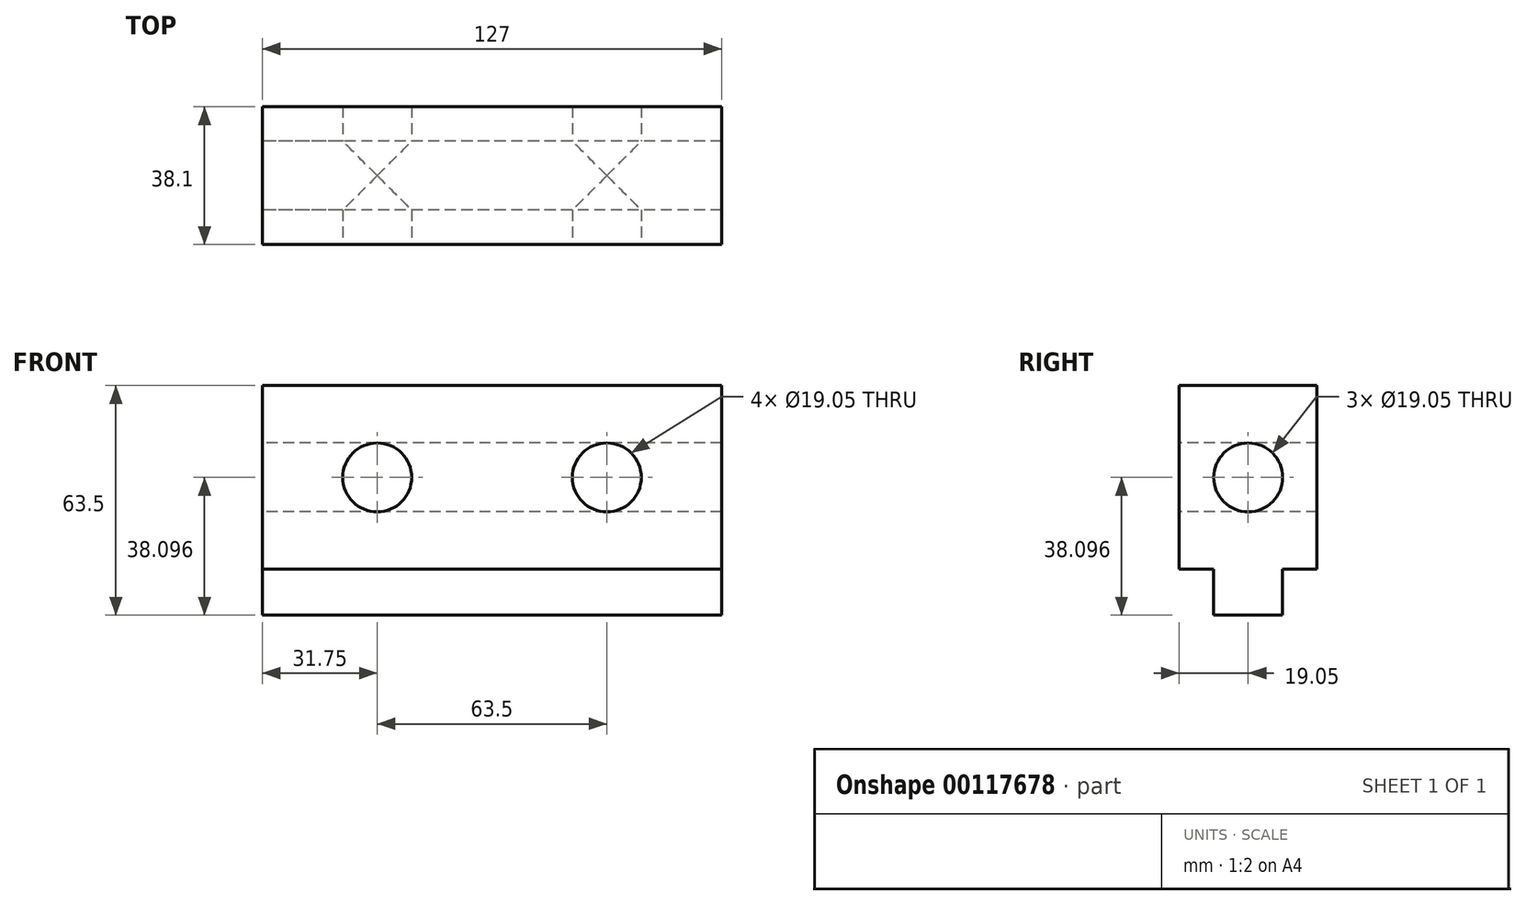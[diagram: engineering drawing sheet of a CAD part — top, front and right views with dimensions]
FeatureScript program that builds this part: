
annotation { "Feature Type Name" : "Feature", "Feature Type Description" : "" }
export const myFeature = defineFeature(function(context is Context, id is Id, definition is map)
    precondition{}
    {
        {
            var Q0;
            Q0=qCreatedBy(makeId("Right.planeOp"),FACE);
            var sketch = newSketch(context, id + "F0", { "sketchPlane" : qUnion([Q0])});
            skLineSegment(sketch, "E0.bottom", {"start": v(-19.05, 38.14) * mm, "end": v(19.05, 38.14) * mm});
            skLineSegment(sketch, "E0.top", {"start": v(-19.05, -25.36) * mm, "end": v(19.05, -25.36) * mm});
            skLineSegment(sketch, "E0.left", {"start": v(-19.05, 38.14) * mm, "end": v(-19.05, -25.36) * mm});
            skLineSegment(sketch, "E0.right", {"start": v(19.05, 38.14) * mm, "end": v(19.05, -25.36) * mm});
            skLineSegment(sketch, "E1", {"start": v(-19.05, 38.14) * mm, "end": v(-19.05, 12.74) * mm});
            skCircle(sketch, "E2", {"center": v(0, 12.74) * mm, "radius": 9.53 * mm});
            skLineSegment(sketch, "E3", {"start": v(-19.05, -25.36) * mm, "end": v(-19.05, -12.66) * mm});
            skLineSegment(sketch, "E4", {"start": v(-19.05, -12.66) * mm, "end": v(-9.53, -12.66) * mm});
            skLineSegment(sketch, "E5", {"start": v(-9.53, -12.66) * mm, "end": v(-9.53, -25.36) * mm});
            skLineSegment(sketch, "E6", {"start": v(19.05, -25.36) * mm, "end": v(19.05, -12.66) * mm});
            skLineSegment(sketch, "E7", {"start": v(19.05, -12.66) * mm, "end": v(9.52, -12.66) * mm});
            skLineSegment(sketch, "E8", {"start": v(9.52, -12.66) * mm, "end": v(9.52, -25.36) * mm});
            skSolve(sketch);
        }
        {
            var Q0;
            Q0=makeQuery(id+"F0.imprint","IMPRINT",FACE,{"disambiguationData":[TD([[makeQuery(id+"F0.imprint","IMPRINT",EDGE,{"derivedFrom":sQuery(id+"F0.wireOp",EDGE,"E0.bottom")}),-1.0]])]});
            extrude(context, id + "F1", {"entities" : qUnion([Q0]), "depth" : 127 * mm});
        }
        {
            var Q0;
            Q0=makeQuery(id+"F1.opExtrude","SWEPT_FACE",FACE,{"disambiguationData":[OSD([sQuery(id+"F0.wireOp",EDGE,"E0.left"),sQuery(id+"F0.wireOp",EDGE,"E1")])]});
            var sketch = newSketch(context, id + "F2", { "sketchPlane" : qUnion([Q0])});
            skLineSegment(sketch, "E9", {"start": v(0, 38.14) * mm, "end": v(31.75, 38.14) * mm});
            skCircle(sketch, "E10", {"center": v(31.75, 12.74) * mm, "radius": 9.53 * mm});
            skLineSegment(sketch, "E11", {"start": v(127, 38.14) * mm, "end": v(95.25, 38.14) * mm});
            skCircle(sketch, "E12", {"center": v(95.25, 12.74) * mm, "radius": 9.53 * mm});
            skSolve(sketch);
        }
        {
            var Q0;
            Q0=sQuery(id+"F2.wireOp",VERTEX,"E12.center");
            var Q1;
            Q1=sQuery(id+"F2.wireOp",VERTEX,"E10.center");
            var Q2;
            Q2=makeQuery(id+"F1.opExtrude","SWEPT_BODY",BODY,{"disambiguationData":[OSD([sQuery(id+"F0.wireOp",EDGE,"E0.bottom"),sQuery(id+"F0.wireOp",EDGE,"E0.top"),sQuery(id+"F0.wireOp",EDGE,"E0.left"),sQuery(id+"F0.wireOp",EDGE,"E0.right"),sQuery(id+"F0.wireOp",EDGE,"E1"),sQuery(id+"F0.wireOp",EDGE,"E2"),sQuery(id+"F0.wireOp",EDGE,"E4"),sQuery(id+"F0.wireOp",EDGE,"E5"),sQuery(id+"F0.wireOp",EDGE,"E7"),sQuery(id+"F0.wireOp",EDGE,"E8")])]});
            hole(context, id + "F3", {"style" : HoleStyle.SIMPLE, "endStyle" : HoleEndStyle.THROUGH, "holeDiameter" : 19.05 * mm, "startFromSketch" : true, "locations" : qUnion([Q0, Q1]), "scope" : qUnion([Q2]), "isTappedThrough" : true});
        }
    });
